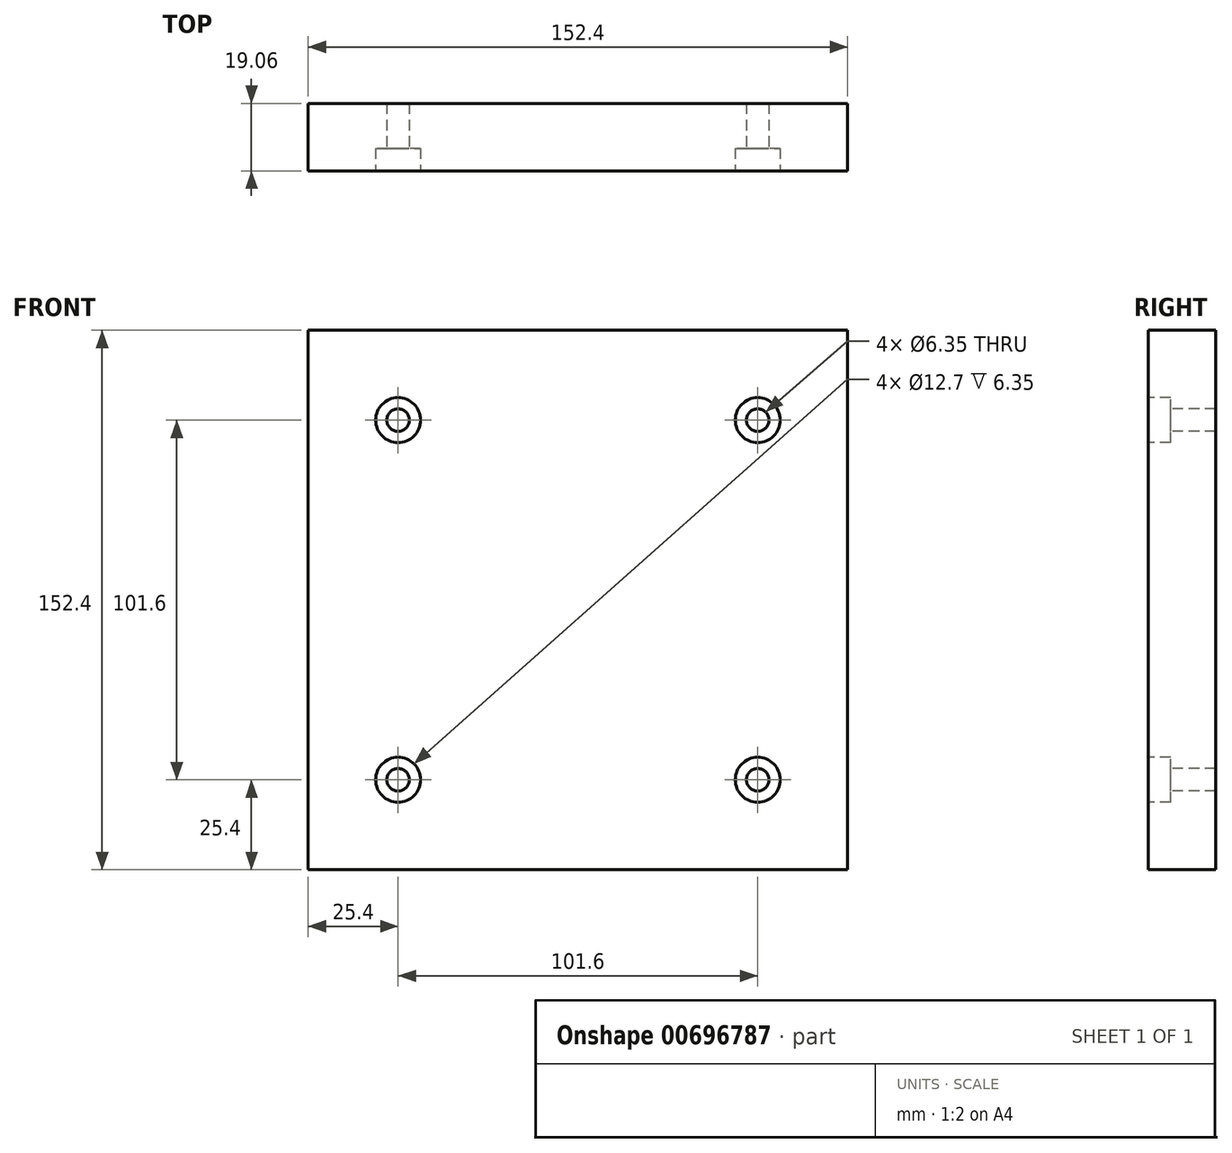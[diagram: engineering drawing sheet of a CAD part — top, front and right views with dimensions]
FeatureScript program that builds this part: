
annotation { "Feature Type Name" : "Feature", "Feature Type Description" : "" }
export const myFeature = defineFeature(function(context is Context, id is Id, definition is map)
    precondition{}
    {
        {
            var Q0;
            Q0=qCreatedBy(makeId("Front.planeOp"),FACE);
            var sketch = newSketch(context, id + "F0", { "sketchPlane" : qUnion([Q0])});
            skLineSegment(sketch, "E0.bottom", {"start": v(76.2, 76.2) * mm, "end": v(-76.2, 76.2) * mm});
            skLineSegment(sketch, "E0.top", {"start": v(76.2, -76.2) * mm, "end": v(-76.2, -76.2) * mm});
            skLineSegment(sketch, "E0.left", {"start": v(76.2, 76.2) * mm, "end": v(76.2, -76.2) * mm});
            skLineSegment(sketch, "E0.right", {"start": v(-76.2, 76.2) * mm, "end": v(-76.2, -76.2) * mm});
            skPoint(sketch, "E0.middle", {"position": v(0, 0) * mm});
            skSolve(sketch);
        }
        {
            var Q0;
            Q0 = qSketchRegion(id + "F0", true);
            extrude(context, id + "F1", {"entities" : qUnion([Q0]), "depth" : 19.05 * mm, "offsetDistance" : 25.4 * mm, "symmetric" : true});
        }
        {
            var Q0;
            Q0=makeQuery(id+"F1.opExtrude","CAP_FACE",FACE,{"disambiguationData":[OSD([sQuery(id+"F0.wireOp",EDGE,"E0.bottom"),sQuery(id+"F0.wireOp",EDGE,"E0.top"),sQuery(id+"F0.wireOp",EDGE,"E0.left"),sQuery(id+"F0.wireOp",EDGE,"E0.right")])],"isStart":false});
            var sketch = newSketch(context, id + "F2", { "sketchPlane" : qUnion([Q0])});
            skLineSegment(sketch, "E1.bottom", {"start": v(50.8, 50.8) * mm, "end": v(-50.8, 50.8) * mm});
            skLineSegment(sketch, "E1.top", {"start": v(50.8, -50.8) * mm, "end": v(-50.8, -50.8) * mm});
            skLineSegment(sketch, "E1.left", {"start": v(50.8, 50.8) * mm, "end": v(50.8, -50.8) * mm});
            skLineSegment(sketch, "E1.right", {"start": v(-50.8, 50.8) * mm, "end": v(-50.8, -50.8) * mm});
            skPoint(sketch, "E1.middle", {"position": v(0, 0) * mm});
            skSolve(sketch);
        }
        {
            var Q0;
            Q0=sQuery(id+"F2.wireOp",VERTEX,"E1.right.start");
            var Q1;
            Q1=sQuery(id+"F2.wireOp",VERTEX,"E1.left.start");
            var Q2;
            Q2=sQuery(id+"F2.wireOp",VERTEX,"E1.left.end");
            var Q3;
            Q3=sQuery(id+"F2.wireOp",VERTEX,"E1.top.end");
            var Q4;
            Q4=makeQuery(id+"F1.opExtrude","SWEPT_BODY",BODY,{"disambiguationData":[OSD([sQuery(id+"F0.wireOp",EDGE,"E0.bottom"),sQuery(id+"F0.wireOp",EDGE,"E0.top"),sQuery(id+"F0.wireOp",EDGE,"E0.left"),sQuery(id+"F0.wireOp",EDGE,"E0.right")])]});
            hole(context, id + "F3", {"style" : HoleStyle.C_BORE, "endStyle" : HoleEndStyle.THROUGH, "holeDiameter" : 6.35 * mm, "cBoreDiameter" : 12.7 * mm, "cBoreDepth" : 6.35 * mm, "majorDiameter" : 6.35 * mm, "isTappedThrough" : true, "tappedDepth" : 12.7 * mm, "tapClearance" : 3, "startFromSketch" : true, "locations" : qUnion([Q0, Q1, Q2, Q3]), "scope" : qUnion([Q4])});
        }
    });
